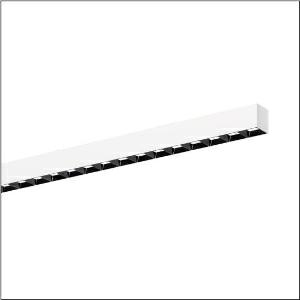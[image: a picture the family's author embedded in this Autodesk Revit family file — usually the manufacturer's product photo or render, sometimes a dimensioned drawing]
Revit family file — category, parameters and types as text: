
# Revit family: silica_r__21_51mx24tctaw_1b94
name_source: partatom
category: Lighting Fixtures
units: mm (PartAtom-declared; Revit-internal decimal feet)

## family parameters
Cut with Voids When Loaded = No
Host = Face
Light Source = No
Part Type = Normal
Room Calculation Point = No
Round Connector Dimension = Use Diameter
Shared = No

## types (1)
- --- (1 x LED, 8200 lm, 81.1 W, 6500K)
    Apparent Load = 81 VA
    CIE Flux Codes = 74 94 99 100 100
    Color Rendering = 80
    Color Temperature = 6500K
    Default Elevation = 1800 mm
    Description = Silica® 21, office luminaire, primary light control with darklight reflector, of PMMA, black, light emission: direct distribution, primary light characteristic: asymmetric, installation type: surface-mounted, LED, rated luminous flux: 8.200lm, luminous efficacy: 96lm/W, light colour: 8tw, colour temperature: 2700..6500K, control gear: ECG DALI, with terminal, 3+2-pole, max. 2.5mm², mains connection: 220..240V, AC, 50/60Hz, rated input power: 85.2W, luminaire housing, of aluminium, traffic white (RAL 9016), length: 3.004mm, width: 53mm, height: 53mm, protection rating (complete): IP20, insulation class (complete): insulation class I (protective earthing), certification: CE, permissible operating ambient temperature: 0..+35°C, standard: EN 50419, packaging unit: 1 piece
    Height = 0 mm  [stored 0 ft]
    Lamp = 1 x LED
    Lamp Light Flux = 8200 lm
    Lamp Power = 81.1 W
    Lamp count = 1
    Length = 3004 mm
    Luminous efficacy = 101 lm/W
    Manufacturer = Siteco
    ModVariant = No
    Model = 51MX24TCTAW
    Mounting Place = Ceiling
    Mounting Type = Recessed
    Number of Poles = 1
    OnlyDefault = Yes
    Power Factor = 1
    Product Name = Silica® 21
    Product group = office luminaire | ceiling recessed
    ProductGroupID = 401
    Protection Class = Protection class I
    Protection Degree = IP 20
    RLX_Detail_Level = 1
    RLX_Emergency_Light_Flux = 0 lm
    RLX_Emergency_Type = 0
    RLX_Emergency_Type_DB = No
    RlxData = <blob elided: 58381 chars, md5=90856f12>
    Socket = socket
    Standby Power = 0 W
    System Light Flux = 8200 lm
    System Power = 81 W
    Type Comments = individual setting
    Type Image = l_1313592.jpg
    URL = http://relux.com
    VarID = @adj_089373
    Voltage = 0 V
    Weight = 0.00 kg
    Width = 53 mm

note: [stored X ft] marks values corroborated as IEEE doubles in the binary element streams (Revit-internal decimal feet)

## geometry (parser evidence)
native form markers: Blend x4, Sweep x11
no freeform markers — native parametric forms only
